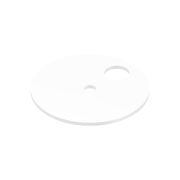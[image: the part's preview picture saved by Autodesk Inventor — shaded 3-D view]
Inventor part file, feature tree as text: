
AUTODESK INVENTOR PART (.ipt)
format: ipt  version: 2012 (Build 160160000, 160)  size: 80,384 bytes
history: native  units: mm
features: extrude x1, sketch x1
ambient origin geometry x8: Origin, YZ Plane, XZ Plane, XY Plane, X Axis, Y Axis, Z Axis, Center Point
feature tree (2):
  extrude  "Extrusion2"  Depth=9.18mm
  sketch  "Sketch1"  dims[d0=94.0mm d1=9.18mm d4=20.0mm d5=30.0mm d6=3.0mm d7=0.0mm]
